# Revit family: Faucet-Deck_Mount-Bath_Filler-KOHLER-FINIAL-K-8785T
name_source: partatom
category: Plumbing Fixtures
revit_build: Autodesk Revit 2017 (Build: 20160225_1515(x64)
units: mm (PartAtom-declared; Revit-internal decimal feet)

## family parameters
Cut with Voids When Loaded = No
Host = Face
OmniClass Number = 23.31.11.00
OmniClass Title = Faucets
Part Type = Normal
Room Calculation Point = No
Round Connector Dimension = Use Diameter
Shared = No

## types (5) — shared parameters
ADA Compliant = No
Assembly Code = D2010
CW Connection = Yes
Cold Water Inlet = Cold Water Inlet
Date Modified = 06/17/2020
Default Elevation = 36"
Description = Finnio Classical handle for bathtub shower mixer
Drain Included = No
Faucet Hole Spacing = 8"
Flow Rate = 2 GPM
HW Connection = Yes
Handle Clearance = 3 13/16"
Height = 17 3/16"
Hot Water Inlet = Hot Water Inlet
Length = 12"
Manufacturer = KOHLER Co.
Master Format 2014 = 22 41 39
Master Format 2014 Name = Residential Faucets, Supplies, and Trim
Material = Solid Metal Construction
Pressure = 45.00 psi
Product Documentation Link = https://files.kohler.com.cn
Product Name = FINIAL
Spout Reach = 12"
URL = http://www.kohler.com.cn
Vent Connection = No
Waste Connection = No
Waste Water Outlet = Waste Water Outlet
WaterSense Certified = No
Width = 15 5/8"

## per-type parameters (varying)
| type | Finish | Handle Material | Model | Product Page URL | Type |
| 4M, CP-Polished Chrome | Kohler-Metal-CP-Polished_Chrome | Kohler-Metal-CP-Polished_Chrome | K-8785T-4M-CP | https://www.kohler.com.cn | 1 |
| 4M, AF-Flange Gold | Kohler-Metal-AF-Flange_Gold | Kohler-Metal-AF-Flange_Gold | K-8785T-4M-AF | https://www.kohler.com.cn | 2 |
| 4M, SN-Champagne Gold | Kohler-Metal-SN-Champagne_Gold | Kohler-Metal-SN-Champagne_Gold | K-8785T-4M-SN | https://www.kohler.com.cn | 3 |
| 4M, BN-Roman Silver | Kohler-Metal-BN-Roman_Silver | Kohler-Metal-BN-Roman_Silver | K-8785T-4M-BN | https://www.kohler.com.cn | 4 |
| 4P, CP-Polished Chrome | Kohler-Metal-CP-Polished_Chrome | Kohler-Silicone-0-White | K-8785T-4P-CP |  | 5 |

## geometry (parser evidence)
native form markers: Sweep x8
no freeform markers — native parametric forms only
